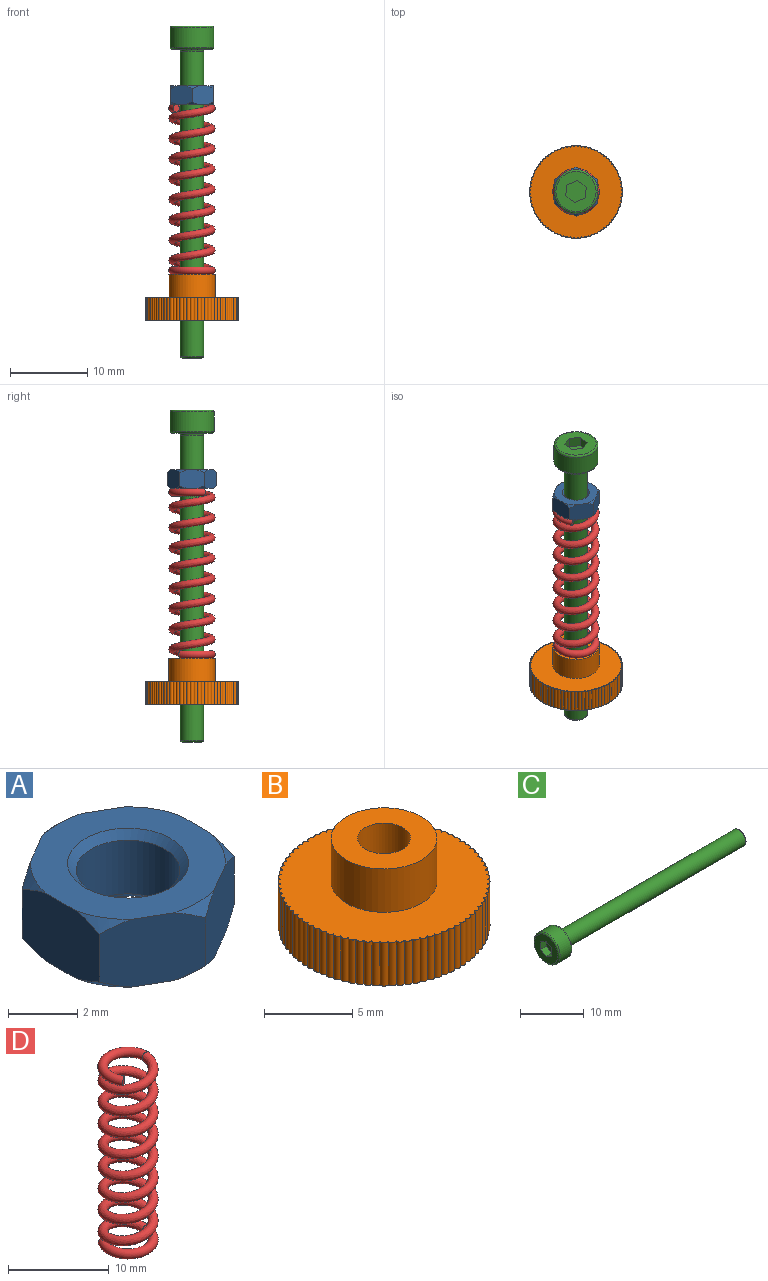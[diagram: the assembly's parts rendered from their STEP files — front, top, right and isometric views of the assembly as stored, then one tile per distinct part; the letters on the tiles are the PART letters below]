
ASSEMBLY  parts=4 mates=4
PART A: 23 faces, bbox 6.3x6.5x2.5 mm
  f0: plane 2.86x2.51mm, normal (0.5,-0.87,0), area 7mm2, adj f1,f5,f6,f7,f11,f14,f21,f22
  f1: plane 3.29x2.51mm, normal (1,0,0), area 7mm2, adj f0,f2,f6,f7,f19,f20,f21,f22
  f2: plane 2.86x2.51mm, normal (0.5,0.87,0), area 7mm2, adj f1,f3,f6,f7,f17,f18,f19,f20
  f3: plane 2.86x2.51mm, normal (-0.5,0.87,0), area 7mm2, adj f2,f4,f6,f7,f15,f16,f17,f18
  f4: plane 3.29x2.51mm, normal (-1,0,0), area 7mm2, adj f3,f5,f6,f7,f12,f13,f15,f16
  f5: plane 2.86x2.51mm, normal (-0.5,-0.87,0), area 7mm2, adj f0,f4,f6,f7,f11,f12,f13,f14
  f6: plane 5.64x5.5mm, normal (0,0,1), area 15mm2, adj f0,f1,f2,f3,f4,f5,f10,f13
  f7: plane 5.64x5.5mm, normal (0,0,-1), area 15mm2, adj f0,f1,f2,f3,f4,f5,f9,f11
  f8: cylinder r=1.5mm len=3mm, axis (0,0,-1), area 17.9mm2, adj f9,f10
  f9: cone r=1.75mm half-angle=45deg, axis (0,0,-1), area 3.6mm2, adj f7,f8
  f10: cone r=1.5mm half-angle=45deg, axis (0,0,1), area 3.6mm2, adj f6,f8
  f11: cone r=3.18mm half-angle=45deg, axis (0,0,1), area 0.4mm2, adj f0,f5,f7
  f12: cone r=3.18mm half-angle=45deg, axis (0,0,1), area 0.4mm2, adj f4,f5,f7
  f13: cone r=2.82mm half-angle=45deg, axis (0,0,-1), area 0.4mm2, adj f4,f5,f6
  f14: cone r=2.82mm half-angle=45deg, axis (0,0,-1), area 0.4mm2, adj f0,f5,f6
  f15: cone r=3.18mm half-angle=45deg, axis (0,0,1), area 0.4mm2, adj f3,f4,f7
  f16: cone r=2.82mm half-angle=45deg, axis (0,0,-1), area 0.4mm2, adj f3,f4,f6
  f17: cone r=3.18mm half-angle=45deg, axis (0,0,1), area 0.4mm2, adj f2,f3,f7
  f18: cone r=2.82mm half-angle=45deg, axis (0,0,-1), area 0.4mm2, adj f2,f3,f6
  f19: cone r=3.18mm half-angle=45deg, axis (0,0,1), area 0.4mm2, adj f1,f2,f7
  f20: cone r=2.82mm half-angle=45deg, axis (0,0,-1), area 0.4mm2, adj f1,f2,f6
  f21: cone r=3.18mm half-angle=45deg, axis (0,0,1), area 0.4mm2, adj f0,f1,f7
  f22: cone r=2.82mm half-angle=45deg, axis (0,0,-1), area 0.4mm2, adj f0,f1,f6
PART B: 85 faces, bbox 12x12x6 mm
  f0: cylinder r=0.25mm len=3mm, axis (0,0,-1), area 1.7mm2, adj f1,f2,f3,f4
  f1: plane 12x12mm, normal (0,0,1), area 83.3mm2, adj f0,f3,f4,f5,f6,f7,f8,f9
  f2: plane 12x12mm, normal (0,0,-1), area 104.5mm2, adj f0,f3,f4,f5,f6,f7,f8,f9
  f3: cylinder r=0.25mm len=3mm, axis (0,0,-1), area 1.7mm2, adj f0,f1,f2,f5
  f4: cylinder r=0.25mm len=3mm, axis (0,0,-1), area 1.7mm2, adj f0,f1,f2,f81
  f5: cylinder r=0.25mm len=3mm, axis (0,0,-1), area 1.7mm2, adj f1,f2,f3,f6
  f6: cylinder r=0.25mm len=3mm, axis (0,0,-1), area 1.7mm2, adj f1,f2,f5,f7
  f7: cylinder r=0.25mm len=3mm, axis (0,0,-1), area 1.7mm2, adj f1,f2,f6,f8
  f8: cylinder r=0.25mm len=3mm, axis (0,0,-1), area 1.7mm2, adj f1,f2,f7,f9
  f9: cylinder r=0.25mm len=3mm, axis (0,0,-1), area 1.7mm2, adj f1,f2,f8,f10
  f10: cylinder r=0.25mm len=3mm, axis (0,0,-1), area 1.7mm2, adj f1,f2,f9,f11
  f11: cylinder r=0.25mm len=3mm, axis (0,0,-1), area 1.7mm2, adj f1,f2,f10,f12
  f12: cylinder r=0.25mm len=3mm, axis (0,0,-1), area 1.7mm2, adj f1,f2,f11,f13
  f13: cylinder r=0.25mm len=3mm, axis (0,0,-1), area 1.7mm2, adj f1,f2,f12,f14
  f14: cylinder r=0.25mm len=3mm, axis (0,0,-1), area 1.7mm2, adj f1,f2,f13,f15
  f15: cylinder r=0.25mm len=3mm, axis (0,0,-1), area 1.7mm2, adj f1,f2,f14,f16
  f16: cylinder r=0.25mm len=3mm, axis (0,0,-1), area 1.7mm2, adj f1,f2,f15,f17
  f17: cylinder r=0.25mm len=3mm, axis (0,0,-1), area 1.7mm2, adj f1,f2,f16,f18
  f18: cylinder r=0.25mm len=3mm, axis (0,0,-1), area 1.7mm2, adj f1,f2,f17,f19
  f19: cylinder r=0.25mm len=3mm, axis (0,0,-1), area 1.7mm2, adj f1,f2,f18,f20
  f20: cylinder r=0.25mm len=3mm, axis (0,0,-1), area 1.7mm2, adj f1,f2,f19,f21
  f21: cylinder r=0.25mm len=3mm, axis (0,0,-1), area 1.7mm2, adj f1,f2,f20,f22
  f22: cylinder r=0.25mm len=3mm, axis (0,0,-1), area 1.7mm2, adj f1,f2,f21,f23
  f23: cylinder r=0.25mm len=3mm, axis (0,0,-1), area 1.7mm2, adj f1,f2,f22,f24
  f24: cylinder r=0.25mm len=3mm, axis (0,0,-1), area 1.7mm2, adj f1,f2,f23,f25
  f25: cylinder r=0.25mm len=3mm, axis (0,0,-1), area 1.7mm2, adj f1,f2,f24,f26
  f26: cylinder r=0.25mm len=3mm, axis (0,0,-1), area 1.7mm2, adj f1,f2,f25,f27
  f27: cylinder r=0.25mm len=3mm, axis (0,0,-1), area 1.7mm2, adj f1,f2,f26,f28
  f28: cylinder r=0.25mm len=3mm, axis (0,0,-1), area 1.7mm2, adj f1,f2,f27,f29
  f29: cylinder r=0.25mm len=3mm, axis (0,0,-1), area 1.7mm2, adj f1,f2,f28,f30
  f30: cylinder r=0.25mm len=3mm, axis (0,0,-1), area 1.7mm2, adj f1,f2,f29,f31
  f31: cylinder r=0.25mm len=3mm, axis (0,0,-1), area 1.7mm2, adj f1,f2,f30,f32
  f32: cylinder r=0.25mm len=3mm, axis (0,0,-1), area 1.7mm2, adj f1,f2,f31,f33
  f33: cylinder r=0.25mm len=3mm, axis (0,0,-1), area 1.7mm2, adj f1,f2,f32,f34
  f34: cylinder r=0.25mm len=3mm, axis (0,0,-1), area 1.7mm2, adj f1,f2,f33,f35
  f35: cylinder r=0.25mm len=3mm, axis (0,0,-1), area 1.7mm2, adj f1,f2,f34,f36
  f36: cylinder r=0.25mm len=3mm, axis (0,0,-1), area 1.7mm2, adj f1,f2,f35,f37
  f37: cylinder r=0.25mm len=3mm, axis (0,0,-1), area 1.7mm2, adj f1,f2,f36,f38
  f38: cylinder r=0.25mm len=3mm, axis (0,0,-1), area 1.7mm2, adj f1,f2,f37,f39
  f39: cylinder r=0.25mm len=3mm, axis (0,0,-1), area 1.7mm2, adj f1,f2,f38,f40
  f40: cylinder r=0.25mm len=3mm, axis (0,0,-1), area 1.7mm2, adj f1,f2,f39,f41
  f41: cylinder r=0.25mm len=3mm, axis (0,0,-1), area 1.7mm2, adj f1,f2,f40,f42
  f42: cylinder r=0.25mm len=3mm, axis (0,0,-1), area 1.7mm2, adj f1,f2,f41,f43
  f43: cylinder r=0.25mm len=3mm, axis (0,0,-1), area 1.7mm2, adj f1,f2,f42,f44
  f44: cylinder r=0.25mm len=3mm, axis (0,0,-1), area 1.7mm2, adj f1,f2,f43,f45
  f45: cylinder r=0.25mm len=3mm, axis (0,0,-1), area 1.7mm2, adj f1,f2,f44,f46
  f46: cylinder r=0.25mm len=3mm, axis (0,0,-1), area 1.7mm2, adj f1,f2,f45,f47
  f47: cylinder r=0.25mm len=3mm, axis (0,0,-1), area 1.7mm2, adj f1,f2,f46,f48
  f48: cylinder r=0.25mm len=3mm, axis (0,0,-1), area 1.7mm2, adj f1,f2,f47,f49
  f49: cylinder r=0.25mm len=3mm, axis (0,0,-1), area 1.7mm2, adj f1,f2,f48,f50
  f50: cylinder r=0.25mm len=3mm, axis (0,0,-1), area 1.7mm2, adj f1,f2,f49,f51
  f51: cylinder r=0.25mm len=3mm, axis (0,0,-1), area 1.7mm2, adj f1,f2,f50,f52
  f52: cylinder r=0.25mm len=3mm, axis (0,0,-1), area 1.7mm2, adj f1,f2,f51,f53
  f53: cylinder r=0.25mm len=3mm, axis (0,0,-1), area 1.7mm2, adj f1,f2,f52,f54
  f54: cylinder r=0.25mm len=3mm, axis (0,0,-1), area 1.7mm2, adj f1,f2,f53,f55
  f55: cylinder r=0.25mm len=3mm, axis (0,0,-1), area 1.7mm2, adj f1,f2,f54,f56
  f56: cylinder r=0.25mm len=3mm, axis (0,0,-1), area 1.7mm2, adj f1,f2,f55,f57
  f57: cylinder r=0.25mm len=3mm, axis (0,0,-1), area 1.7mm2, adj f1,f2,f56,f58
  f58: cylinder r=0.25mm len=3mm, axis (0,0,-1), area 1.7mm2, adj f1,f2,f57,f59
  f59: cylinder r=0.25mm len=3mm, axis (0,0,-1), area 1.7mm2, adj f1,f2,f58,f60
  f60: cylinder r=0.25mm len=3mm, axis (0,0,-1), area 1.7mm2, adj f1,f2,f59,f61
  f61: cylinder r=0.25mm len=3mm, axis (0,0,-1), area 1.7mm2, adj f1,f2,f60,f62
  f62: cylinder r=0.25mm len=3mm, axis (0,0,-1), area 1.7mm2, adj f1,f2,f61,f63
  f63: cylinder r=0.25mm len=3mm, axis (0,0,-1), area 1.7mm2, adj f1,f2,f62,f64
  f64: cylinder r=0.25mm len=3mm, axis (0,0,-1), area 1.7mm2, adj f1,f2,f63,f65
  f65: cylinder r=0.25mm len=3mm, axis (0,0,-1), area 1.7mm2, adj f1,f2,f64,f66
  f66: cylinder r=0.25mm len=3mm, axis (0,0,-1), area 1.7mm2, adj f1,f2,f65,f67
  f67: cylinder r=0.25mm len=3mm, axis (0,0,-1), area 1.7mm2, adj f1,f2,f66,f68
  f68: cylinder r=0.25mm len=3mm, axis (0,0,-1), area 1.7mm2, adj f1,f2,f67,f69
  f69: cylinder r=0.25mm len=3mm, axis (0,0,-1), area 1.7mm2, adj f1,f2,f68,f70
  f70: cylinder r=0.25mm len=3mm, axis (0,0,-1), area 1.7mm2, adj f1,f2,f69,f71
  f71: cylinder r=0.25mm len=3mm, axis (0,0,-1), area 1.7mm2, adj f1,f2,f70,f72
  f72: cylinder r=0.25mm len=3mm, axis (0,0,-1), area 1.7mm2, adj f1,f2,f71,f73
  f73: cylinder r=0.25mm len=3mm, axis (0,0,-1), area 1.7mm2, adj f1,f2,f72,f74
  f74: cylinder r=0.25mm len=3mm, axis (0,0,-1), area 1.7mm2, adj f1,f2,f73,f75
  f75: cylinder r=0.25mm len=3mm, axis (0,0,-1), area 1.7mm2, adj f1,f2,f74,f76
  f76: cylinder r=0.25mm len=3mm, axis (0,0,-1), area 1.7mm2, adj f1,f2,f75,f77
  f77: cylinder r=0.25mm len=3mm, axis (0,0,-1), area 1.7mm2, adj f1,f2,f76,f78
  f78: cylinder r=0.25mm len=3mm, axis (0,0,-1), area 1.7mm2, adj f1,f2,f77,f79
  f79: cylinder r=0.25mm len=3mm, axis (0,0,-1), area 1.7mm2, adj f1,f2,f78,f80
  f80: cylinder r=0.25mm len=3mm, axis (0,0,-1), area 1.7mm2, adj f1,f2,f79,f81
  f81: cylinder r=0.25mm len=3mm, axis (0,0,-1), area 1.7mm2, adj f1,f2,f4,f80
  f82: cylinder r=3mm len=6mm, axis (0,0,-1), area 56.5mm2, adj f1,f83
  f83: plane 6x6mm, normal (0,0,1), area 21.2mm2, adj f82,f84
  f84: cylinder r=1.5mm len=6mm, axis (0,0,1), area 56.5mm2, adj f2,f83
PART C: 16 faces, bbox 43x6.2x6.2 mm
  f0: plane 5.2x5.2mm, normal (-1,0,0), area 15.8mm2, adj f5,f6,f7,f8,f9,f10,f12
  f1: cylinder r=2.85mm len=5.7mm, axis (-1,0,0), area 44.8mm2, adj f12,f13
  f2: plane 5.2x5.2mm, normal (1,0,0), area 11.6mm2, adj f13,f14
  f3: cylinder r=1.5mm len=39.5mm, axis (-1,0,0), area 372.3mm2, adj f14,f15
  f4: plane 2.5x2.5mm, normal (1,0,0), area 4.9mm2, adj f15
  f5: plane 1.3x1.25mm, normal (0,-0.5,0.87), area 1.9mm2, adj f0,f6,f10,f11
  f6: plane 1.3x1.25mm, normal (0,0.5,0.87), area 1.9mm2, adj f0,f5,f7,f11
  f7: plane 1.44x1.3mm, normal (0,1,0), area 1.9mm2, adj f0,f6,f8,f11
  f8: plane 1.3x1.25mm, normal (0,0.5,-0.87), area 1.9mm2, adj f0,f7,f9,f11
  f9: plane 1.3x1.25mm, normal (0,-0.5,-0.87), area 1.9mm2, adj f0,f8,f10,f11
  f10: plane 1.44x1.3mm, normal (0,-1,0), area 1.9mm2, adj f0,f5,f9,f11
  f11: plane 2.89x2.5mm, normal (-1,0,0), area 5.4mm2, adj f5,f6,f7,f8,f9,f10
  f12: torus R=2.6mm, axis (-1,0,0), area 6.8mm2, adj f0,f1
  f13: torus R=2.6mm, axis (-1,0,0), area 6.8mm2, adj f1,f2
  f14: torus R=1.75mm, axis (-1,0,0), area 3.9mm2, adj f2,f3
  f15: torus R=1.25mm, axis (-1,0,0), area 3.5mm2, adj f3,f4
PART D: 5 faces, bbox 7x8.1x22 mm
  f0: bspline ~22x8.08mm, area 398.8mm2, adj f2,f4
  f1: plane 1x0.82mm, normal (0.57,-0.82,0), area 0.8mm2, adj f2
  f2: torus R=2.5mm, axis (0,0,1), area 29.5mm2, adj f0,f1
  f3: plane 1x0.82mm, normal (0.57,0.82,0), area 0.8mm2, adj f4
  f4: torus R=2.5mm, axis (0,0,-1), area 29.5mm2, adj f0,f3
PLACE A t=(14.2,18.79,36.98)mm
PLACE B t=(14.2,18.79,8.98)mm
PLACE C rot(axis=(-0.69,0.23,0.69),154deg) t=(14.2,18.79,44.14)mm
PLACE D t=(14.2,18.79,15.48)mm fixed
MATE cylindrical B.f84 <-> C.f1  axis (0,0,1) through (14.2,18.79,11.98)mm
MATE planar A.f7 <-> D.f2  axis (0,0,-1) through (11.45,18.16,36.98)mm
MATE cylindrical C.f1 <-> A.f8  axis (0,0,-1) through (14.2,18.79,44.14)mm
MATE cylindrical C.f1 <-> D.f2  axis (0,0,1) through (14.2,18.79,24.14)mm
